# Revit family: Power-ModularDevices-GEWISS-90AM-SPD_TYPE2_1P
name_source: partatom
category: Apparecchi elettrici
revit_build: Autodesk Revit 2016 (Build: 20161004_0715(x64)
units: mm (PartAtom-declared; Revit-internal decimal feet)

## family parameters
Condiviso = No
Host = Superficie
Mantenere orientamento annotazione = Sì
Numero OmniClass = 23.80.50.00
Punto di calcolo locali = Sì
Quota connettore circolare = Usa diametro
Taglio con vuoti quando caricato = No
Tipo di parte = Normale
Titolo OmniClass = Terminals for Power Supply

## types (3) — shared parameters
Catalogue = POWER
Catalogue Range = 90 AM
Electrocod = 0642
IDF = fd5a9a67-0f8f-4116-b411-a5605e20defb
IDT = efe6c794-a624-4260-8996-be3dd57c760e
Immagine tipo = GWD6411.jpg
Maximum discharge current: = 40KA
No. Chorus modules = 1
No. of modules EN 50022 = 1
No. of poles = 1P
Number of poles = 1P
Numero di poli = 1
Produttore = GEWISS S.p.A.
Prospetto di default = 1219 mm
SEO = Limiter
Spostamento_x = -340 mm
Technical sheet = https://www.gewiss.com
Type = 2
Type: = 2
URL = https://www.gewiss.com
Version file RFA = 18.0
carico = Altro
potenza in watt = 0 V

## per-type parameters (varying)
| type | Descrizione | EAN code | Modello | Rated voltage | Rated voltage AC |
| GWD6413 - LST - SPD 1P 40KA 400V T2 | LST - SPD 1P 40KA 400V T2 | 8011564774889 | GWD6413 | 400Vac | 400V |
| GWD6412 - LST - SPD 1P 40KA AUX. T2 | LST - SPD 1P 40KA AUX. T2 | 8011564774872 | GWD6412 | 230Vac | 230V |
| GWD6411 - LST - SPD 1P 40KA T2 | LST - SPD 1P 40KA T2 | 8011564774865 | GWD6411 | 230Vac | 230V |
